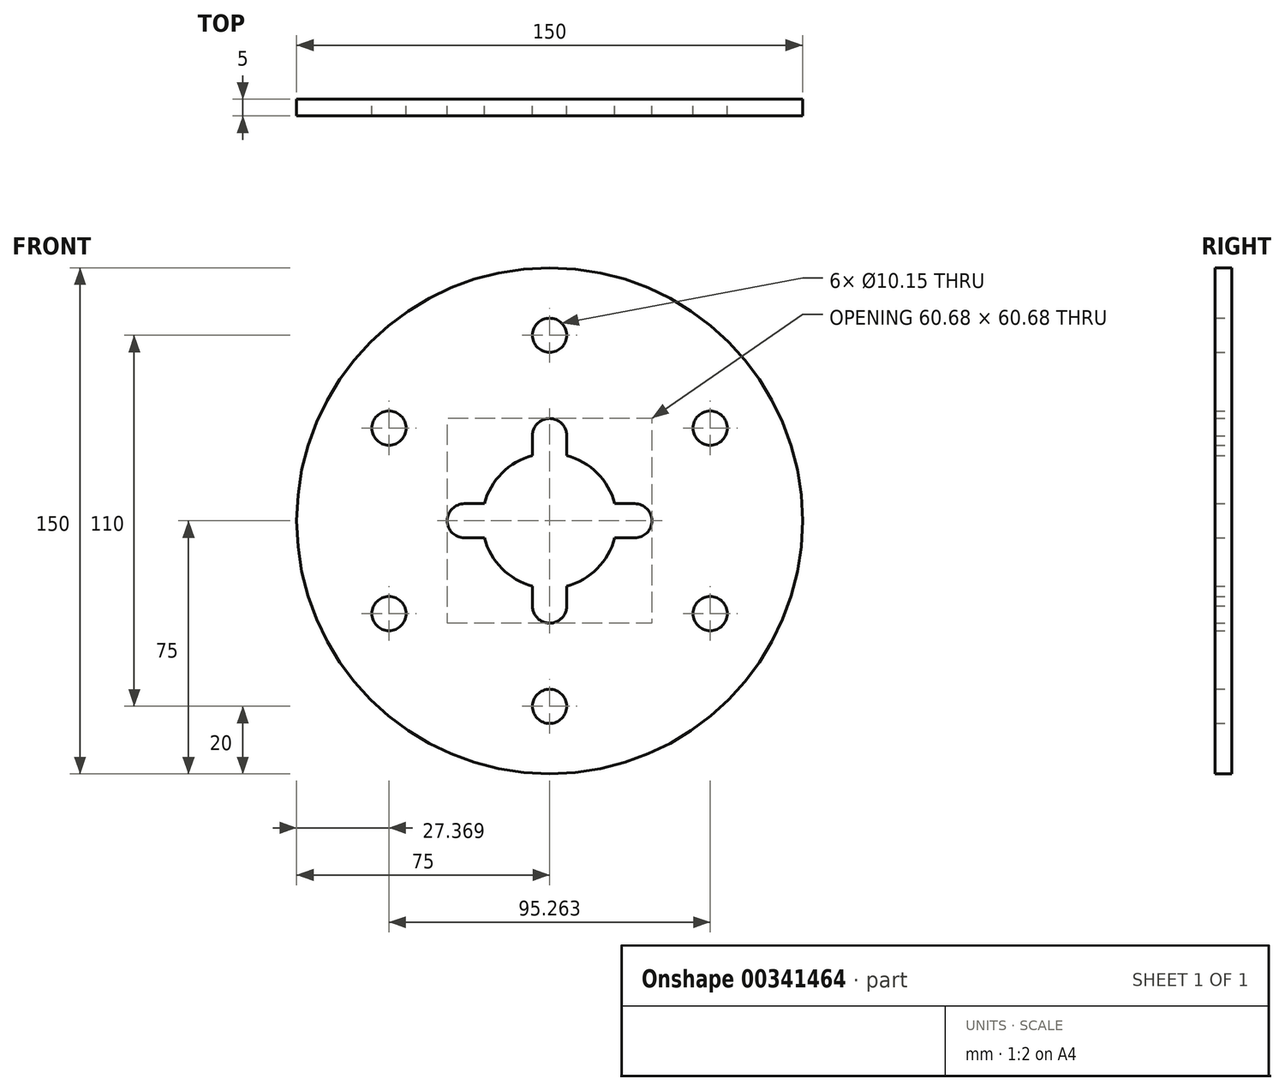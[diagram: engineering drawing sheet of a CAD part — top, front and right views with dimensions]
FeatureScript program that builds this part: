
annotation { "Feature Type Name" : "Feature", "Feature Type Description" : "" }
export const myFeature = defineFeature(function(context is Context, id is Id, definition is map)
    precondition{}
    {
        {
            var Q0;
            Q0=qCreatedBy(makeId("Front.planeOp"),FACE);
            var sketch = newSketch(context, id + "F0", { "sketchPlane" : qUnion([Q0])});
            skCircle(sketch, "E0", {"center": v(0, 0) * mm, "radius": 75 * mm});
            skArc(sketch, "E1", {"start": v(-5.07, 19.35) * mm, "mid": v(-14.14, 14.14) * mm, "end": v(-19.35, 5.07) * mm});
            skCircle(sketch, "E2", {"center": v(0, 0) * mm, "radius": 30 * mm, "construction": true});
            skArc(sketch, "E3", {"start": v(5.07, 25.21) * mm, "mid": v(0, 30.34) * mm, "end": v(-5.07, 25.21) * mm});
            skArc(sketch, "E4.1.0", {"start": v(-25.27, 5.07) * mm, "mid": v(-30.34, 0) * mm, "end": v(-25.27, -5.07) * mm});
            skArc(sketch, "E4.2.0", {"start": v(-5.07, -25.21) * mm, "mid": v(-0.03, -30.34) * mm, "end": v(5.07, -25.27) * mm});
            skArc(sketch, "E5.1.3.0", {"start": v(25.27, -5.07) * mm, "mid": v(30.34, 0) * mm, "end": v(25.27, 5.07) * mm});
            skLineSegment(sketch, "E6", {"start": v(-5.07, 25.21) * mm, "end": v(-5.07, 19.35) * mm});
            skLineSegment(sketch, "E7", {"start": v(5.07, 25.21) * mm, "end": v(5, 19.36) * mm});
            skLineSegment(sketch, "E8", {"start": v(-25.27, 5.07) * mm, "end": v(-19.35, 5.07) * mm});
            skLineSegment(sketch, "E9", {"start": v(-25.27, -5.07) * mm, "end": v(-19.35, -5.07) * mm});
            skLineSegment(sketch, "E10", {"start": v(-5.07, -25.27) * mm, "end": v(-5.07, -19.35) * mm});
            skLineSegment(sketch, "E11", {"start": v(5.07, -25.27) * mm, "end": v(5.07, -19.35) * mm});
            skLineSegment(sketch, "E12", {"start": v(25.27, -5.07) * mm, "end": v(19.35, -5.07) * mm});
            skLineSegment(sketch, "E13", {"start": v(25.27, 5.07) * mm, "end": v(19.35, 5.07) * mm});
            skArc(sketch, "E14.trimOffspring", {"start": v(-19.35, -5.07) * mm, "mid": v(-14.14, -14.14) * mm, "end": v(-5.07, -19.35) * mm});
            skArc(sketch, "E15.trimOffspring", {"start": v(19.35, 5.07) * mm, "mid": v(14.12, 14.17) * mm, "end": v(5, 19.36) * mm});
            skArc(sketch, "E16.trimOffspring", {"start": v(5.07, -19.35) * mm, "mid": v(14.14, -14.14) * mm, "end": v(19.35, -5.07) * mm});
            skCircle(sketch, "E17", {"center": v(0, 55) * mm, "radius": 5.07 * mm});
            skCircle(sketch, "E18.1.0", {"center": v(-47.63, 27.5) * mm, "radius": 5.07 * mm});
            skCircle(sketch, "E18.2.0", {"center": v(-47.63, -27.5) * mm, "radius": 5.07 * mm});
            skCircle(sketch, "E18.3.0", {"center": v(0, -55) * mm, "radius": 5.07 * mm});
            skCircle(sketch, "E18.4.0", {"center": v(47.63, -27.5) * mm, "radius": 5.07 * mm});
            skCircle(sketch, "E18.5.0", {"center": v(47.63, 27.5) * mm, "radius": 5.07 * mm});
            skCircle(sketch, "E19", {"center": v(0, 0) * mm, "radius": 54.84 * mm, "construction": true});
            skSolve(sketch);
        }
        {
            var Q0;
            Q0 = qSketchRegion(id + "F0", true);
            extrude(context, id + "F1", {"entities" : qUnion([Q0]), "depth" : 5 * mm});
        }
    });
